# Revit family: POR_Matura2_S6486_BIM_FR
name_source: partatom
category: Plumbing Fixtures
revit_build: Autodesk Revit 2017 (Build: 20160225_1515(x64)
units: mm (PartAtom-declared; Revit-internal decimal feet)

## family parameters
Always vertical = No
Cut with Voids When Loaded = No
OmniClass Number = 23.45.05.14.17
OmniClass Title = Showers
Part Type = Normal
Room Calculation Point = No
Round Connector Dimension = Use Diameter
Shared = No
Work Plane-Based = No

## types (1)
- S6486AA - MATURA 2 - Barre de maintien
    Accessoires = http://www.porcher.com
    Auteur = Ideal Standard
    BIMobject main category = Sanitary
    BIMobject main category code = sanitary
    BOSUseNativeGeometries = 1
    Bim-NomDuProjet = POR_Porcher_Accessories_S6486AA
    Brand url = http://www.porcher.com
    Caractéristiques = Barre de maintien - 45 cm
    CodeBarre = 5017830387367
    Conformité = NF
    ConseilsDInstallation = www.idealspec.fr
    Cost = 0 $
    Couleur = Chrome
    CoûtDeRemplacement = 0
    Date of publishing = 2018_05_23
    DateDeCréation = 2018_05_23
    Description = MATURA 2 - Barre de maintien
    Dimensions = 456 x 84 x 118mm
    DuréeGarantie = ans
    DétailGarantie = Constructeur
    EAN code = https://5017830387367
    Edition number = 1
    Espace = Interne
    Forme = Complexe
    Hauteur = 456 mm
    IFC Classification = Sanitary Terminal
    IfcExportAs = IfcSanitaryTerminalType
    IfcExportType = Accessories
    InformationsProduit = www.idealspec.fr
    Installation instructions = http://www.idealspec.fr
    Largeur = 84 mm  [stored 0.275591 ft]
    Longueur = 118 mm
    Manufacturer name = Porcher
    Marque = PORCHER
    Model = S6486AA
    NBS Reference Code = 31-75
    NBS Reference Description = Sanitary Accessories
    Nom = POR_Porcher_Accessories_S6486AA
    Nominal height = 95
    Nominal width = 540
    OmniClass Code = 23-31 25 00
    OmniClass Description = Toilet and Bath Specialties
    PerformanceAccessibilité = NF
    PoidsNet = 3.16 Kg
    Product Guid = 602070c2-1e13-4f99-9576-13fba314c996
    Product SKU = S6486
    Product certification = http://www.idealspec.fr
    Product data url = https://bimobject.com
    Product family = MATURA 2
    Product group = Accessories
    Product name = MATURA 2 - Barre de maintien
    Product url = http://www.idealspec.fr
    Profondeur = 0 mm  [stored 0 ft]
    QR code = http://bimobject.com
    Raccordement = Plomberie
    Référence = S6486AA
    Révision = 1
    Technical description = http://www.idealspec.fr
    TypeDImmobilisation = Fixe
    URL = http://www.porcher.com
    Uniclass 2015 Code = Pr_40_20_76
    Uniclass 2015 Name = Sanitary accessories
    Uniclass2015Code = Pr_40_20_76
    Uniclass2015Title = Sanitary accessories
    Uniclass2015Version = Products v1.1
    UnitéDeTemps = an
    UrlDuFabricant = http://www.porcher.com
    Version = 1
    Weight Net (Kg) = 3.16

note: [stored X ft] marks values corroborated as IEEE doubles in the binary element streams (Revit-internal decimal feet)

## geometry (parser evidence)
native form markers: Sweep x3
no freeform markers — native parametric forms only
